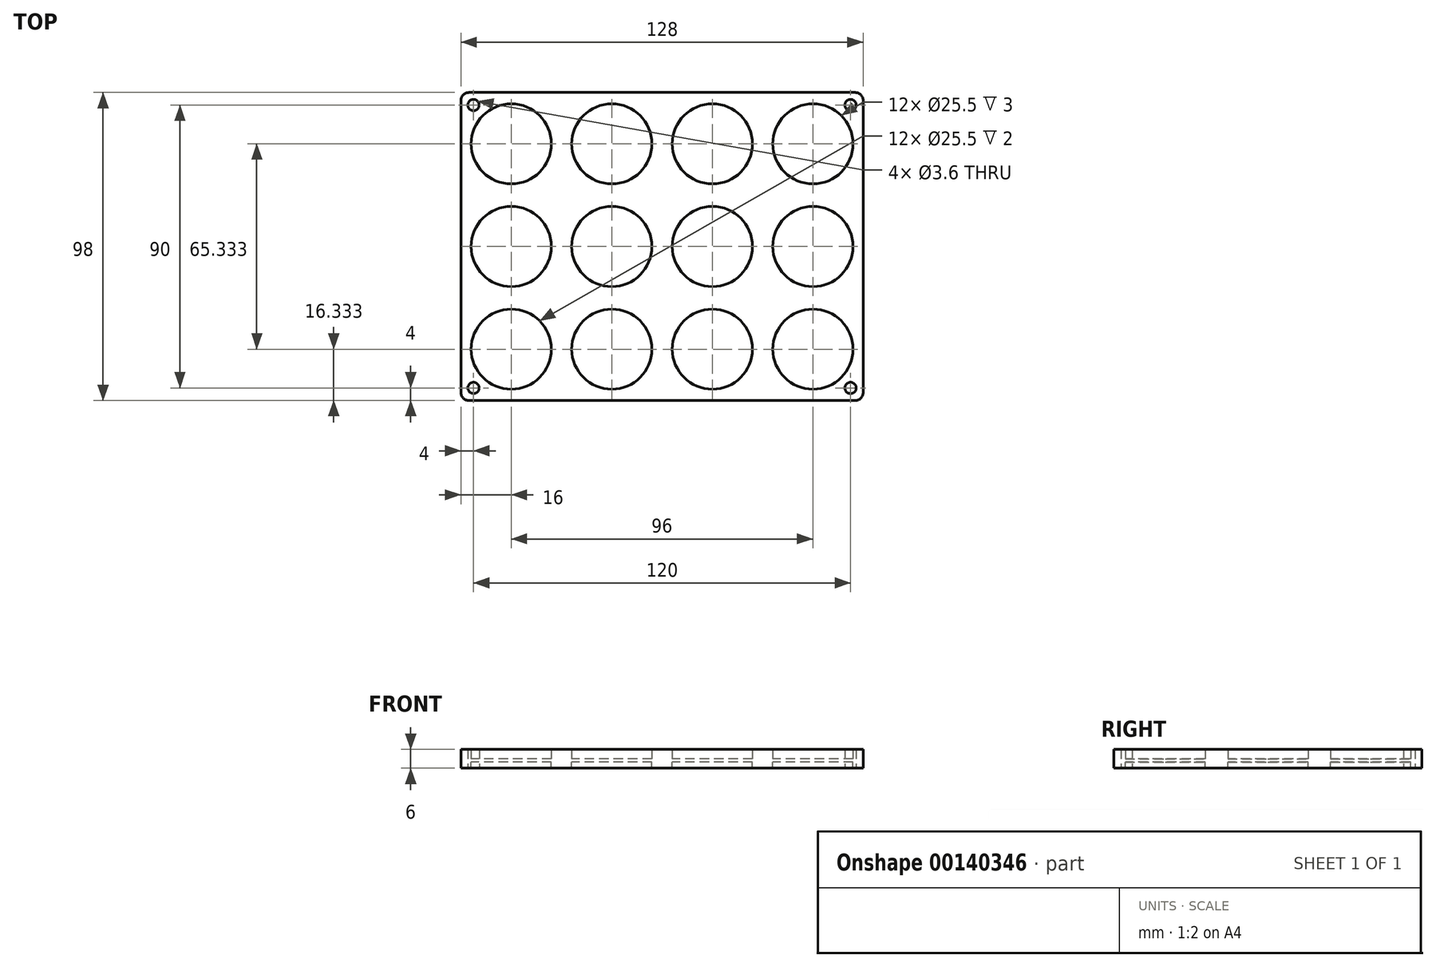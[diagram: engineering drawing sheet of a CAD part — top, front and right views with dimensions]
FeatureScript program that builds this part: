
annotation { "Feature Type Name" : "Feature", "Feature Type Description" : "" }
export const myFeature = defineFeature(function(context is Context, id is Id, definition is map)
    precondition{}
    {
        {
            assignVariable(context, id + "F0", {"name" : "thickness", "anyValue" : 3});
        }
        {
            var Q0;
            Q0=qCreatedBy(makeId("Top.planeOp"),FACE);
            var sketch = newSketch(context, id + "F1", { "sketchPlane" : qUnion([Q0])});
            skLineSegment(sketch, "E0.bottom", {"start": v(64, 49) * mm, "end": v(-64, 49) * mm});
            skLineSegment(sketch, "E0.top", {"start": v(64, -49) * mm, "end": v(-64, -49) * mm});
            skLineSegment(sketch, "E0.left", {"start": v(64, 49) * mm, "end": v(64, -49) * mm});
            skLineSegment(sketch, "E0.right", {"start": v(-64, 49) * mm, "end": v(-64, -49) * mm});
            skPoint(sketch, "E0.middle", {"position": v(0, 0) * mm});
            skLineSegment(sketch, "E1", {"start": v(48, 49) * mm, "end": v(48, -49) * mm, "construction": true});
            skLineSegment(sketch, "E2", {"start": v(-48, 49) * mm, "end": v(-48, -49) * mm, "construction": true});
            skLineSegment(sketch, "E3", {"start": v(-16, 49) * mm, "end": v(-16, -49) * mm, "construction": true});
            skLineSegment(sketch, "E4", {"start": v(16, 49) * mm, "end": v(16, -49) * mm, "construction": true});
            skLineSegment(sketch, "E5", {"start": v(-64, 32.67) * mm, "end": v(64, 32.67) * mm, "construction": true});
            skLineSegment(sketch, "E6", {"start": v(-64, -32.67) * mm, "end": v(64, -32.67) * mm, "construction": true});
            skCircle(sketch, "E7", {"center": v(-48, 32.67) * mm, "radius": 12.75 * mm});
            skCircle(sketch, "E8", {"center": v(-16, 32.67) * mm, "radius": 12.75 * mm});
            skCircle(sketch, "E9", {"center": v(16, 32.67) * mm, "radius": 12.75 * mm});
            skCircle(sketch, "E10", {"center": v(48, 32.67) * mm, "radius": 12.75 * mm});
            skLineSegment(sketch, "E11", {"start": v(-64, 0) * mm, "end": v(64, 0) * mm, "construction": true});
            skCircle(sketch, "E12", {"center": v(-48, 0) * mm, "radius": 12.75 * mm});
            skCircle(sketch, "E13", {"center": v(-16, 0) * mm, "radius": 12.75 * mm});
            skCircle(sketch, "E14", {"center": v(16, 0) * mm, "radius": 12.75 * mm});
            skCircle(sketch, "E15", {"center": v(48, 0) * mm, "radius": 12.75 * mm});
            skCircle(sketch, "E16", {"center": v(48, -32.67) * mm, "radius": 12.75 * mm});
            skCircle(sketch, "E17", {"center": v(16, -32.67) * mm, "radius": 12.75 * mm});
            skCircle(sketch, "E18", {"center": v(-16, -32.67) * mm, "radius": 12.75 * mm});
            skCircle(sketch, "E19", {"center": v(-48, -32.67) * mm, "radius": 12.75 * mm});
            skLineSegment(sketch, "E20.bottom", {"start": v(-60, 45) * mm, "end": v(60, 45) * mm, "construction": true});
            skLineSegment(sketch, "E20.top", {"start": v(-60, -45) * mm, "end": v(60, -45) * mm, "construction": true});
            skLineSegment(sketch, "E20.left", {"start": v(-60, 45) * mm, "end": v(-60, -45) * mm, "construction": true});
            skLineSegment(sketch, "E20.right", {"start": v(60, 45) * mm, "end": v(60, -45) * mm, "construction": true});
            skCircle(sketch, "E21", {"center": v(-60, 45) * mm, "radius": 1.8 * mm});
            skCircle(sketch, "E22", {"center": v(60, 45) * mm, "radius": 1.8 * mm});
            skCircle(sketch, "E23", {"center": v(-60, -45) * mm, "radius": 1.8 * mm});
            skCircle(sketch, "E24", {"center": v(60, -45) * mm, "radius": 1.8 * mm});
            skArc(sketch, "E25", {"start": v(-54, 49) * mm, "mid": v(-71.07, 56.07) * mm, "end": v(-64, 39) * mm});
            skArc(sketch, "E26", {"start": v(-64, -39) * mm, "mid": v(-71.07, -56.07) * mm, "end": v(-54, -49) * mm});
            skArc(sketch, "E27", {"start": v(54, -49) * mm, "mid": v(71.07, -56.07) * mm, "end": v(64, -39) * mm});
            skArc(sketch, "E28.trimOffspring", {"start": v(64, 37.2) * mm, "mid": v(69.07, 54.07) * mm, "end": v(52.2, 49) * mm});
            skSolve(sketch);
        }
        {
            var Q0;
            Q0=makeQuery(id+"F1.imprint","IMPRINT",FACE,{"disambiguationData":[TD([[makeQuery(id+"F1.imprint","IMPRINT",EDGE,{"derivedFrom":sQuery(id+"F1.wireOp",EDGE,"E0.bottom")}),1.0]])]});
            extrude(context, id + "F2", {"entities" : qUnion([Q0]), "depth" : (getVariable(context, 'thickness')) * mm});
        }
        {
            var Q0;
            Q0=makeQuery(id+"F1.imprint","IMPRINT",FACE,{"disambiguationData":[TD([[makeQuery(id+"F1.imprint","IMPRINT",EDGE,{"derivedFrom":sQuery(id+"F1.wireOp",EDGE,"E0.bottom")}),1.0]])]});
            extrude(context, id + "F3", {"entities" : qUnion([Q0]), "oppositeDirection" : true, "depth" : (getVariable(context, 'thickness')) * mm});
        }
        {
            var Q0;
            Q0=makeQuery(id+"F1.imprint","IMPRINT",FACE,{"disambiguationData":[TD([[makeQuery(id+"F1.imprint","IMPRINT",EDGE,{"derivedFrom":sQuery(id+"F1.wireOp",EDGE,"E8")}),1.0]])]});
            var Q1;
            Q1=makeQuery(id+"F1.imprint","IMPRINT",FACE,{"disambiguationData":[TD([[makeQuery(id+"F1.imprint","IMPRINT",EDGE,{"derivedFrom":sQuery(id+"F1.wireOp",EDGE,"E13")}),1.0]])]});
            var Q2;
            Q2=makeQuery(id+"F1.imprint","IMPRINT",FACE,{"disambiguationData":[TD([[makeQuery(id+"F1.imprint","IMPRINT",EDGE,{"derivedFrom":sQuery(id+"F1.wireOp",EDGE,"E18")}),1.0]])]});
            var Q3;
            Q3=makeQuery(id+"F1.imprint","IMPRINT",FACE,{"disambiguationData":[TD([[makeQuery(id+"F1.imprint","IMPRINT",EDGE,{"derivedFrom":sQuery(id+"F1.wireOp",EDGE,"E19")}),1.0]])]});
            var Q4;
            Q4=makeQuery(id+"F1.imprint","IMPRINT",FACE,{"disambiguationData":[TD([[makeQuery(id+"F1.imprint","IMPRINT",EDGE,{"derivedFrom":sQuery(id+"F1.wireOp",EDGE,"E12")}),1.0]])]});
            var Q5;
            Q5=makeQuery(id+"F1.imprint","IMPRINT",FACE,{"disambiguationData":[TD([[makeQuery(id+"F1.imprint","IMPRINT",EDGE,{"derivedFrom":sQuery(id+"F1.wireOp",EDGE,"E7")}),1.0]])]});
            var Q6;
            Q6=makeQuery(id+"F1.imprint","IMPRINT",FACE,{"disambiguationData":[TD([[makeQuery(id+"F1.imprint","IMPRINT",EDGE,{"derivedFrom":sQuery(id+"F1.wireOp",EDGE,"E9")}),1.0]])]});
            var Q7;
            Q7=makeQuery(id+"F1.imprint","IMPRINT",FACE,{"disambiguationData":[TD([[makeQuery(id+"F1.imprint","IMPRINT",EDGE,{"derivedFrom":sQuery(id+"F1.wireOp",EDGE,"E14")}),1.0]])]});
            var Q8;
            Q8=makeQuery(id+"F1.imprint","IMPRINT",FACE,{"disambiguationData":[TD([[makeQuery(id+"F1.imprint","IMPRINT",EDGE,{"derivedFrom":sQuery(id+"F1.wireOp",EDGE,"E17")}),1.0]])]});
            var Q9;
            Q9=makeQuery(id+"F1.imprint","IMPRINT",FACE,{"disambiguationData":[TD([[makeQuery(id+"F1.imprint","IMPRINT",EDGE,{"derivedFrom":sQuery(id+"F1.wireOp",EDGE,"E10")}),1.0]])]});
            var Q10;
            Q10=makeQuery(id+"F1.imprint","IMPRINT",FACE,{"disambiguationData":[TD([[makeQuery(id+"F1.imprint","IMPRINT",EDGE,{"derivedFrom":sQuery(id+"F1.wireOp",EDGE,"E15")}),1.0]])]});
            var Q11;
            Q11=makeQuery(id+"F1.imprint","IMPRINT",FACE,{"disambiguationData":[TD([[makeQuery(id+"F1.imprint","IMPRINT",EDGE,{"derivedFrom":sQuery(id+"F1.wireOp",EDGE,"E16")}),1.0]])]});
            extrude(context, id + "F4", {"entities" : qUnion([Q0, Q1, Q2, Q3, Q4, Q5, Q6, Q7, Q8, Q9, Q10, Q11]), "operationType" : NewBodyOperationType.ADD, "oppositeDirection" : true, "depth" : 1 * mm});
        }
        {
            var Q0;
            Q0=makeQuery(id+"F3.opExtrude","SWEPT_EDGE",EDGE,{"disambiguationData":[OSD([sQuery(id+"F1.wireOp",EDGE,"E0.bottom"),sQuery(id+"F1.wireOp",EDGE,"E0.right")])]});
            var Q1;
            Q1=makeQuery(id+"F2.opExtrude","SWEPT_EDGE",EDGE,{"disambiguationData":[OSD([sQuery(id+"F1.wireOp",EDGE,"E0.bottom"),sQuery(id+"F1.wireOp",EDGE,"E0.right")])]});
            var Q2;
            Q2=makeQuery(id+"F2.opExtrude","SWEPT_EDGE",EDGE,{"disambiguationData":[OSD([sQuery(id+"F1.wireOp",EDGE,"E0.top"),sQuery(id+"F1.wireOp",EDGE,"E0.right")])]});
            var Q3;
            Q3=makeQuery(id+"F3.opExtrude","SWEPT_EDGE",EDGE,{"disambiguationData":[OSD([sQuery(id+"F1.wireOp",EDGE,"E0.top"),sQuery(id+"F1.wireOp",EDGE,"E0.right")])]});
            var Q4;
            Q4=makeQuery(id+"F3.opExtrude","SWEPT_EDGE",EDGE,{"disambiguationData":[OSD([sQuery(id+"F1.wireOp",EDGE,"E0.top"),sQuery(id+"F1.wireOp",EDGE,"E0.left")])]});
            var Q5;
            Q5=makeQuery(id+"F2.opExtrude","SWEPT_EDGE",EDGE,{"disambiguationData":[OSD([sQuery(id+"F1.wireOp",EDGE,"E0.top"),sQuery(id+"F1.wireOp",EDGE,"E0.left")])]});
            var Q6;
            Q6=makeQuery(id+"F3.opExtrude","SWEPT_EDGE",EDGE,{"disambiguationData":[OSD([sQuery(id+"F1.wireOp",EDGE,"E0.bottom"),sQuery(id+"F1.wireOp",EDGE,"E0.left")])]});
            var Q7;
            Q7=makeQuery(id+"F2.opExtrude","SWEPT_EDGE",EDGE,{"disambiguationData":[OSD([sQuery(id+"F1.wireOp",EDGE,"E0.bottom"),sQuery(id+"F1.wireOp",EDGE,"E0.left")])]});
            fillet(context, id + "F5", {"entities" : qUnion([Q0, Q1, Q2, Q3, Q4, Q5, Q6, Q7]), "radius" : 2.5 * mm, "tangentPropagation" : true, "allowEdgeOverflow" : false});
        }
    });
